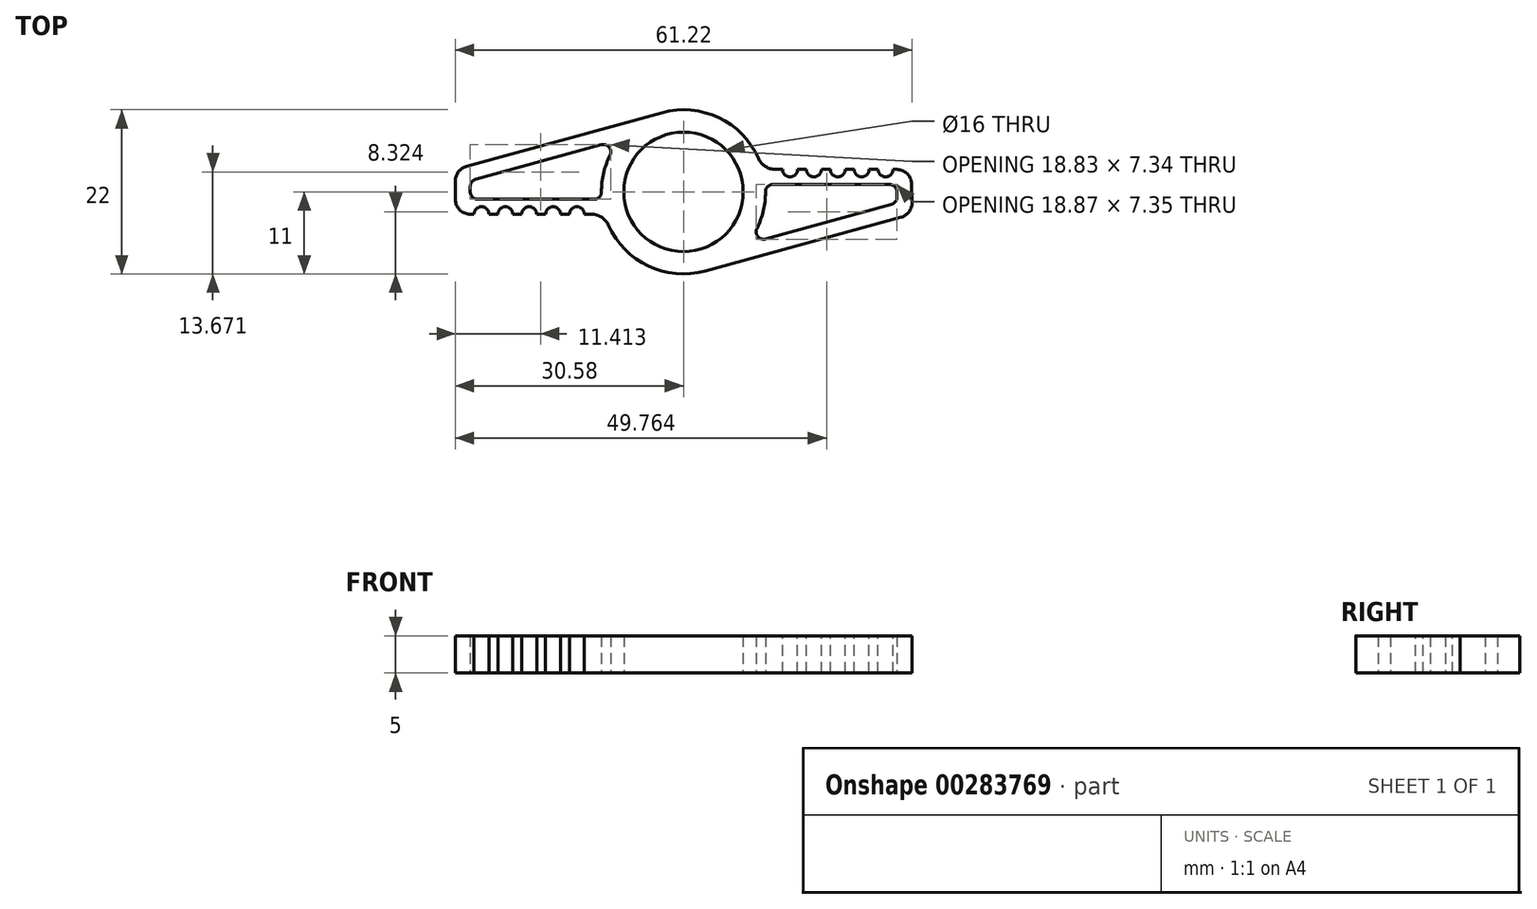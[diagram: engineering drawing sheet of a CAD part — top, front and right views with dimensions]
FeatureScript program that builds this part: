
annotation { "Feature Type Name" : "Feature", "Feature Type Description" : "" }
export const myFeature = defineFeature(function(context is Context, id is Id, definition is map)
    precondition{}
    {
        {
            var Q0;
            Q0=qCreatedBy(makeId("Top.planeOp"),FACE);
            var sketch = newSketch(context, id + "F0", { "sketchPlane" : qUnion([Q0])});
            skCircle(sketch, "E0", {"center": v(0, 0) * mm, "radius": 8 * mm});
            skArc(sketch, "E1", {"start": v(-9.85, 4.9) * mm, "mid": v(-10.7, 2.52) * mm, "end": v(-11, 0) * mm});
            skLineSegment(sketch, "E2", {"start": v(-30, 0) * mm, "end": v(30, 0) * mm, "construction": true});
            skLineSegment(sketch, "E3.0.left", {"start": v(12.33, 3) * mm, "end": v(28.58, 3) * mm});
            skLineSegment(sketch, "E3.0.right", {"start": v(-28.58, -3) * mm, "end": v(-12.33, -3) * mm});
            skLineSegment(sketch, "E4", {"start": v(-29.11, 3.4) * mm, "end": v(-2.92, 10.6) * mm});
            skLineSegment(sketch, "E5", {"start": v(29.17, -3.41) * mm, "end": v(2.9, -10.6) * mm});
            skLineSegment(sketch, "E6", {"start": v(-30.58, 1.48) * mm, "end": v(-30.58, -1) * mm});
            skLineSegment(sketch, "E7", {"start": v(30.58, 1.04) * mm, "end": v(30.64, -1.44) * mm});
            skPoint(sketch, "E8.visualSharp", {"position": v(-30.58, 3) * mm});
            skArc(sketch, "E8.filletArc", {"start": v(-29.11, 3.4) * mm, "mid": v(-30.17, 2.69) * mm, "end": v(-30.58, 1.48) * mm});
            skPoint(sketch, "E9.visualSharp", {"position": v(-30.58, -3) * mm});
            skArc(sketch, "E9.filletArc", {"start": v(-30.58, -1) * mm, "mid": v(-30, -2.41) * mm, "end": v(-28.58, -3) * mm});
            skPoint(sketch, "E10.visualSharp", {"position": v(30.67, -3) * mm});
            skArc(sketch, "E10.filletArc", {"start": v(29.17, -3.41) * mm, "mid": v(30.24, -2.68) * mm, "end": v(30.64, -1.44) * mm});
            skPoint(sketch, "E11.visualSharp", {"position": v(30.54, 3) * mm});
            skArc(sketch, "E11.filletArc", {"start": v(30.58, 1.04) * mm, "mid": v(29.98, 2.43) * mm, "end": v(28.58, 3) * mm});
            skLineSegment(sketch, "E12.0", {"start": v(27.89, -1.7) * mm, "end": v(11, -6.32) * mm});
            skLineSegment(sketch, "E12.1", {"start": v(28.6, 0.02) * mm, "end": v(28.62, -0.7) * mm});
            skLineSegment(sketch, "E12.2", {"start": v(12, 1) * mm, "end": v(27.6, 1) * mm});
            skLineSegment(sketch, "E13.0", {"start": v(-27.85, 1.68) * mm, "end": v(-11.01, 6.3) * mm});
            skLineSegment(sketch, "E13.1", {"start": v(-28.58, 0.71) * mm, "end": v(-28.58, 0) * mm});
            skLineSegment(sketch, "E13.2", {"start": v(-27.58, -1) * mm, "end": v(-12, -1) * mm});
            skArc(sketch, "E14.trimOffspring", {"start": v(-10.05, -4.48) * mm, "mid": v(-4.7, -9.94) * mm, "end": v(2.9, -10.6) * mm});
            skArc(sketch, "E15.trimOffspring", {"start": v(10.05, 4.48) * mm, "mid": v(4.7, 9.95) * mm, "end": v(-2.92, 10.6) * mm});
            skArc(sketch, "E16.trimOffspring", {"start": v(9.85, -4.9) * mm, "mid": v(10.7, -2.52) * mm, "end": v(11, 0) * mm});
            skPoint(sketch, "E17.visualSharp", {"position": v(-8.48, 7) * mm});
            skArc(sketch, "E17.filletArc", {"start": v(-9.85, 4.9) * mm, "mid": v(-9.97, 5.98) * mm, "end": v(-11.01, 6.3) * mm});
            skPoint(sketch, "E18.visualSharp", {"position": v(-10.95, -1) * mm});
            skArc(sketch, "E18.filletArc", {"start": v(-12, -1) * mm, "mid": v(-11.3, -0.7) * mm, "end": v(-11, 0) * mm});
            skArc(sketch, "E19.filletArc", {"start": v(-27.85, 1.68) * mm, "mid": v(-28.38, 1.32) * mm, "end": v(-28.58, 0.71) * mm});
            skArc(sketch, "E20.filletArc", {"start": v(-28.58, 0) * mm, "mid": v(-28.3, -0.7) * mm, "end": v(-27.58, -1) * mm});
            skPoint(sketch, "E21.visualSharp", {"position": v(10.95, 1) * mm});
            skArc(sketch, "E21.filletArc", {"start": v(12, 1) * mm, "mid": v(11.3, 0.7) * mm, "end": v(11, 0) * mm});
            skPoint(sketch, "E22.visualSharp", {"position": v(8.48, -7) * mm});
            skArc(sketch, "E22.filletArc", {"start": v(9.85, -4.9) * mm, "mid": v(9.97, -5.99) * mm, "end": v(11, -6.32) * mm});
            skArc(sketch, "E23.filletArc", {"start": v(27.89, -1.7) * mm, "mid": v(28.42, -1.32) * mm, "end": v(28.62, -0.7) * mm});
            skArc(sketch, "E24.filletArc", {"start": v(28.6, 0.02) * mm, "mid": v(28.3, 0.71) * mm, "end": v(27.6, 1) * mm});
            skPoint(sketch, "E25.visualSharp", {"position": v(-10.58, -3) * mm});
            skArc(sketch, "E25.filletArc", {"start": v(-10.05, -4.48) * mm, "mid": v(-10.97, -3.4) * mm, "end": v(-12.33, -3) * mm});
            skPoint(sketch, "E26.visualSharp", {"position": v(10.58, 3) * mm});
            skArc(sketch, "E26.filletArc", {"start": v(10.05, 4.48) * mm, "mid": v(10.97, 3.4) * mm, "end": v(12.33, 3) * mm});
            skSolve(sketch);
        }
        {
            var Q0;
            Q0=makeQuery(id+"F0.imprint","IMPRINT",FACE,{"disambiguationData":[TD([[makeQuery(id+"F0.imprint","IMPRINT",EDGE,{"derivedFrom":sQuery(id+"F0.wireOp",EDGE,"E0")}),-1.0]])]});
            extrude(context, id + "F1", {"entities" : qUnion([Q0]), "depth" : 5 * mm, "offsetDistance" : 25 * mm});
        }
        {
            var Q0;
            Q0=makeQuery(id+"F1.opExtrude","CAP_FACE",FACE,{"disambiguationData":[OSD([sQuery(id+"F0.wireOp",EDGE,"E0"),sQuery(id+"F0.wireOp",EDGE,"E1"),sQuery(id+"F0.wireOp",EDGE,"E3.0.left"),sQuery(id+"F0.wireOp",EDGE,"E3.0.right"),sQuery(id+"F0.wireOp",EDGE,"E4"),sQuery(id+"F0.wireOp",EDGE,"E5"),sQuery(id+"F0.wireOp",EDGE,"E6"),sQuery(id+"F0.wireOp",EDGE,"E7"),sQuery(id+"F0.wireOp",EDGE,"E8.filletArc"),sQuery(id+"F0.wireOp",EDGE,"E9.filletArc"),sQuery(id+"F0.wireOp",EDGE,"E10.filletArc"),sQuery(id+"F0.wireOp",EDGE,"E11.filletArc"),sQuery(id+"F0.wireOp",EDGE,"E12.0"),sQuery(id+"F0.wireOp",EDGE,"E12.1"),sQuery(id+"F0.wireOp",EDGE,"E12.2"),sQuery(id+"F0.wireOp",EDGE,"E13.0"),sQuery(id+"F0.wireOp",EDGE,"E13.1"),sQuery(id+"F0.wireOp",EDGE,"E13.2"),sQuery(id+"F0.wireOp",EDGE,"E14.trimOffspring"),sQuery(id+"F0.wireOp",EDGE,"E15.trimOffspring"),sQuery(id+"F0.wireOp",EDGE,"E16.trimOffspring"),sQuery(id+"F0.wireOp",EDGE,"E17.filletArc"),sQuery(id+"F0.wireOp",EDGE,"E18.filletArc"),sQuery(id+"F0.wireOp",EDGE,"E19.filletArc"),sQuery(id+"F0.wireOp",EDGE,"E20.filletArc"),sQuery(id+"F0.wireOp",EDGE,"E21.filletArc"),sQuery(id+"F0.wireOp",EDGE,"E22.filletArc"),sQuery(id+"F0.wireOp",EDGE,"E23.filletArc"),sQuery(id+"F0.wireOp",EDGE,"E24.filletArc"),sQuery(id+"F0.wireOp",EDGE,"E25.filletArc"),sQuery(id+"F0.wireOp",EDGE,"E26.filletArc")])],"isStart":false});
            var sketch = newSketch(context, id + "F2", { "sketchPlane" : qUnion([Q0])});
            skCircle(sketch, "E27", {"center": v(-27.08, -3) * mm, "radius": 1 * mm});
            skCircle(sketch, "E28.1.0.0", {"center": v(-23.88, -3) * mm, "radius": 1 * mm});
            skCircle(sketch, "E28.2.0.0", {"center": v(-20.68, -3) * mm, "radius": 1 * mm});
            skCircle(sketch, "E28.3.0.0", {"center": v(-17.48, -3) * mm, "radius": 1 * mm});
            skCircle(sketch, "E28.4.0.0", {"center": v(-14.28, -3) * mm, "radius": 1 * mm});
            skLineSegment(sketch, "E28.direction1", {"start": v(-27.08, -3) * mm, "end": v(-23.88, -3) * mm, "construction": true});
            skCircle(sketch, "E29", {"center": v(27.08, 3) * mm, "radius": 1 * mm});
            skCircle(sketch, "E30.1.0.0", {"center": v(23.88, 3) * mm, "radius": 1 * mm});
            skCircle(sketch, "E30.2.0.0", {"center": v(20.68, 3) * mm, "radius": 1 * mm});
            skCircle(sketch, "E30.3.0.0", {"center": v(17.48, 3) * mm, "radius": 1 * mm});
            skCircle(sketch, "E30.4.0.0", {"center": v(14.28, 3) * mm, "radius": 1 * mm});
            skLineSegment(sketch, "E30.direction1", {"start": v(27.08, 3) * mm, "end": v(23.88, 3) * mm, "construction": true});
            skPoint(sketch, "E31.center", {"position": v(0, 0) * mm});
            skSolve(sketch);
        }
        {
            var Q0;
            Q0 = qSketchRegion(id + "F2", true);
            extrude(context, id + "F3", {"entities" : qUnion([Q0]), "operationType" : NewBodyOperationType.REMOVE, "oppositeDirection" : true, "depth" : 25 * mm, "offsetDistance" : 25 * mm});
        }
    });
